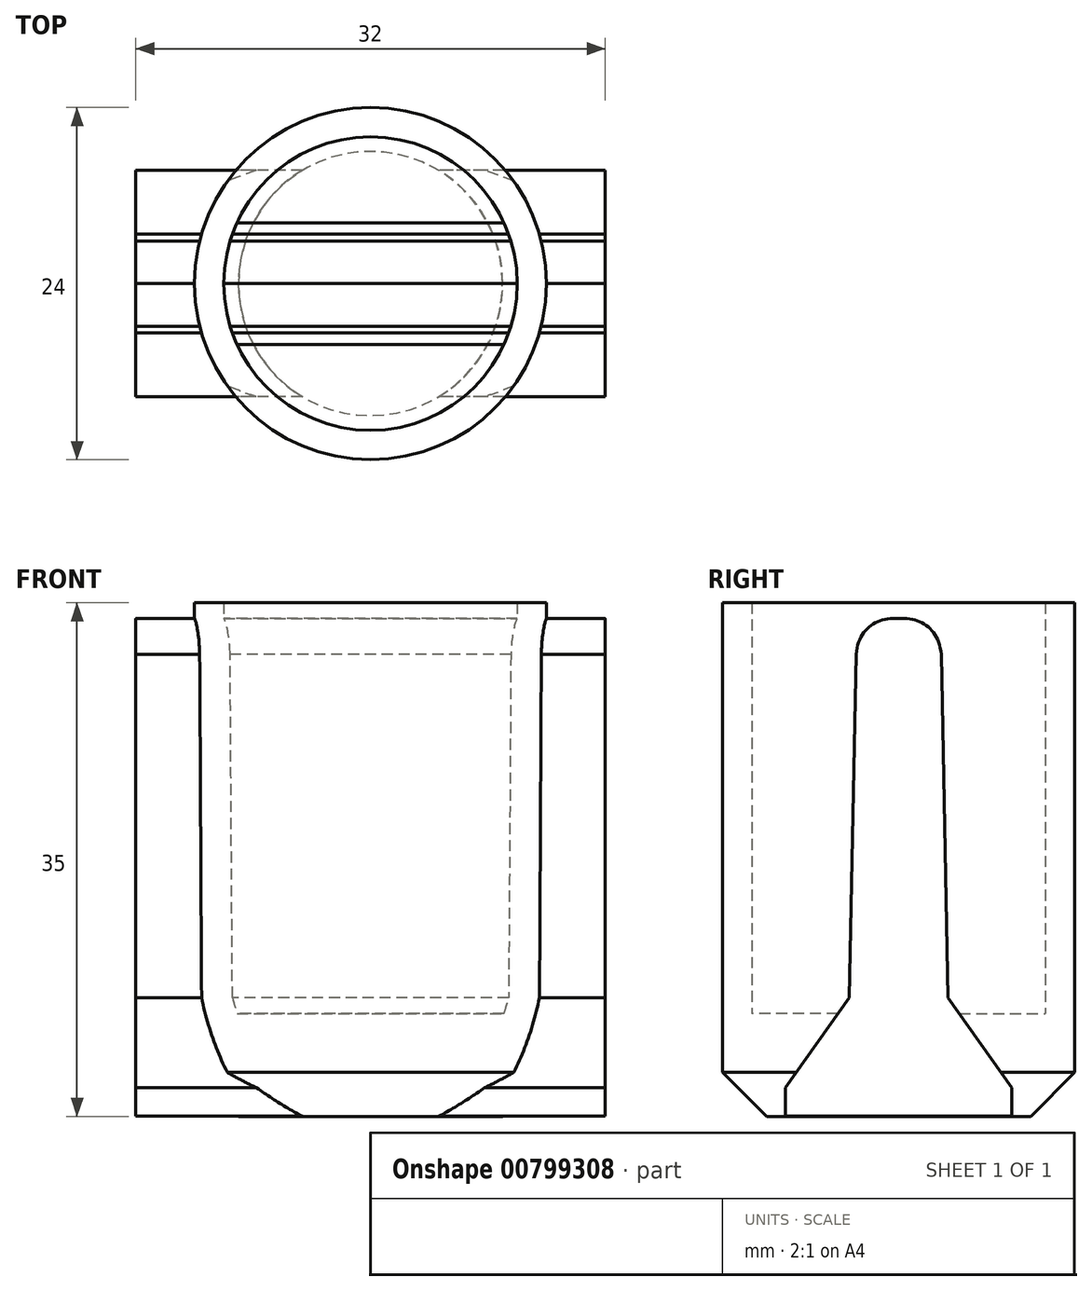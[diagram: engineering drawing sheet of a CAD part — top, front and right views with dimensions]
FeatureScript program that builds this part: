
annotation { "Feature Type Name" : "Feature", "Feature Type Description" : "" }
export const myFeature = defineFeature(function(context is Context, id is Id, definition is map)
    precondition{}
    {
        {
            var Q0;
            Q0=qCreatedBy(makeId("Top.planeOp"),FACE);
            var sketch = newSketch(context, id + "F0", { "sketchPlane" : qUnion([Q0])});
            skCircle(sketch, "E0", {"center": v(0, 0) * mm, "radius": 10 * mm});
            skCircle(sketch, "E1.0", {"center": v(0, 0) * mm, "radius": 12 * mm});
            skSolve(sketch);
        }
        {
            var Q0;
            Q0=makeQuery(id+"F0.imprint","IMPRINT",FACE,{"disambiguationData":[TD([[makeQuery(id+"F0.imprint","IMPRINT",EDGE,{"derivedFrom":sQuery(id+"F0.wireOp",EDGE,"E0")}),1.0]])]});
            extrude(context, id + "F1", {"entities" : qUnion([Q0]), "depth" : 2 * mm, "offsetDistance" : 25 * mm});
        }
        {
            var Q0;
            Q0 = qSketchRegion(id + "F0", true);
            extrude(context, id + "F2", {"entities" : qUnion([Q0]), "operationType" : NewBodyOperationType.ADD, "depth" : 30 * mm, "offsetDistance" : 25 * mm});
        }
        {
            var Q0;
            {var subQ0=sQuery(id+"F0.wireOp",EDGE,"E0");Q0=makeQuery(id+"F2.boolean.opBoolean","MERGE",FACE,{"derivedFrom":[makeQuery(id+"F1.opExtrude","CAP_FACE",FACE,{"disambiguationData":[OSD([subQ0])],"isStart":true}),makeQuery(id+"F2.opExtrude","CAP_FACE",FACE,{"disambiguationData":[OSD([subQ0,sQuery(id+"F0.wireOp",EDGE,"E1.0")])],"isStart":true})]});}
            extrude(context, id + "F3", {"entities" : qUnion([Q0]), "operationType" : NewBodyOperationType.ADD, "depth" : 5 * mm, "offsetDistance" : 25 * mm});
        }
        {
            var Q0;
            Q0=makeQuery(id+"F3.opExtrude","CAP_EDGE",EDGE,{"disambiguationData":[OSD([sQuery(id+"F0.wireOp",EDGE,"E1.0")])],"isStart":false});
            chamfer(context, id + "F4", {"entities" : qUnion([Q0]), "width" : 3 * mm, "tangentPropagation" : true});
        }
        {
            var Q0;
            Q0=qCreatedBy(makeId("Right.planeOp"),FACE);
            var sketch = newSketch(context, id + "F5", { "sketchPlane" : qUnion([Q0])});
            skFitSpline(sketch, "E2", {"points": [v(0, 28.93) * mm, v(-2.9, 26.48) * mm], "startDerivative": vector(-4.54, 0.28) * mm, "endDerivative": vector(-0.55, -5.37) * mm});
            skLineSegment(sketch, "E3", {"start": v(-2.9, 26.48) * mm, "end": v(-3.37, 3.1) * mm});
            skLineSegment(sketch, "E4", {"start": v(-7.72, -4.99) * mm, "end": v(0, -4.99) * mm});
            skLineSegment(sketch, "E5", {"start": v(0, -4.99) * mm, "end": v(0, 28.93) * mm});
            skFitSpline(sketch, "E6.MirrorCS", {"points": [v(0, 28.93) * mm, v(2.9, 26.48) * mm], "startDerivative": vector(4.54, 0.28) * mm, "endDerivative": vector(0.55, -5.37) * mm});
            skLineSegment(sketch, "E7.MirrorCS", {"start": v(2.9, 26.48) * mm, "end": v(3.37, 3.1) * mm});
            skLineSegment(sketch, "E8.MirrorCS", {"start": v(7.72, -4.99) * mm, "end": v(0, -4.99) * mm});
            skLineSegment(sketch, "E9", {"start": v(-7.72, -4.99) * mm, "end": v(-7.72, -3.05) * mm});
            skLineSegment(sketch, "E10", {"start": v(-7.72, -3.05) * mm, "end": v(-3.37, 3.1) * mm});
            skLineSegment(sketch, "E11.MirrorCS", {"start": v(7.72, -3.05) * mm, "end": v(3.37, 3.1) * mm});
            skLineSegment(sketch, "E12.MirrorCS", {"start": v(7.72, -4.99) * mm, "end": v(7.72, -3.05) * mm});
            skSolve(sketch);
        }
        {
            var Q0;
            Q0 = qSketchRegion(id + "F5", true);
            extrude(context, id + "F6", {"entities" : qUnion([Q0]), "operationType" : NewBodyOperationType.ADD, "endBound" : BoundingType.SYMMETRIC, "depth" : 32 * mm, "offsetDistance" : 25 * mm});
        }
    });
